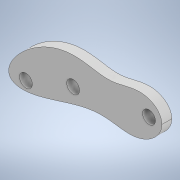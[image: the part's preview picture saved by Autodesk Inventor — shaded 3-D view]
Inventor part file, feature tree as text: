
AUTODESK INVENTOR PART (.ipt)
format: ipt  version: 2022 (Build 260153000, 153)  size: 126,464 bytes
history: native  units: in
note: dims shown in document units (in); Inventor stores cm internally (conversion verified against a paired STEP export)
features: extrude x1, sketch x1
ambient origin geometry x8: Origin, YZ Plane, XZ Plane, XY Plane, X Axis, Y Axis, Z Axis, Center Point
bodies: Body1 (feature_tree)
feature tree (2):
  extrude  "Extrusion1"  Depth=0.2559in
  sketch  "Sketch2"  dims[d0=0.1969in d1=0.0in d2=0.2559in]
